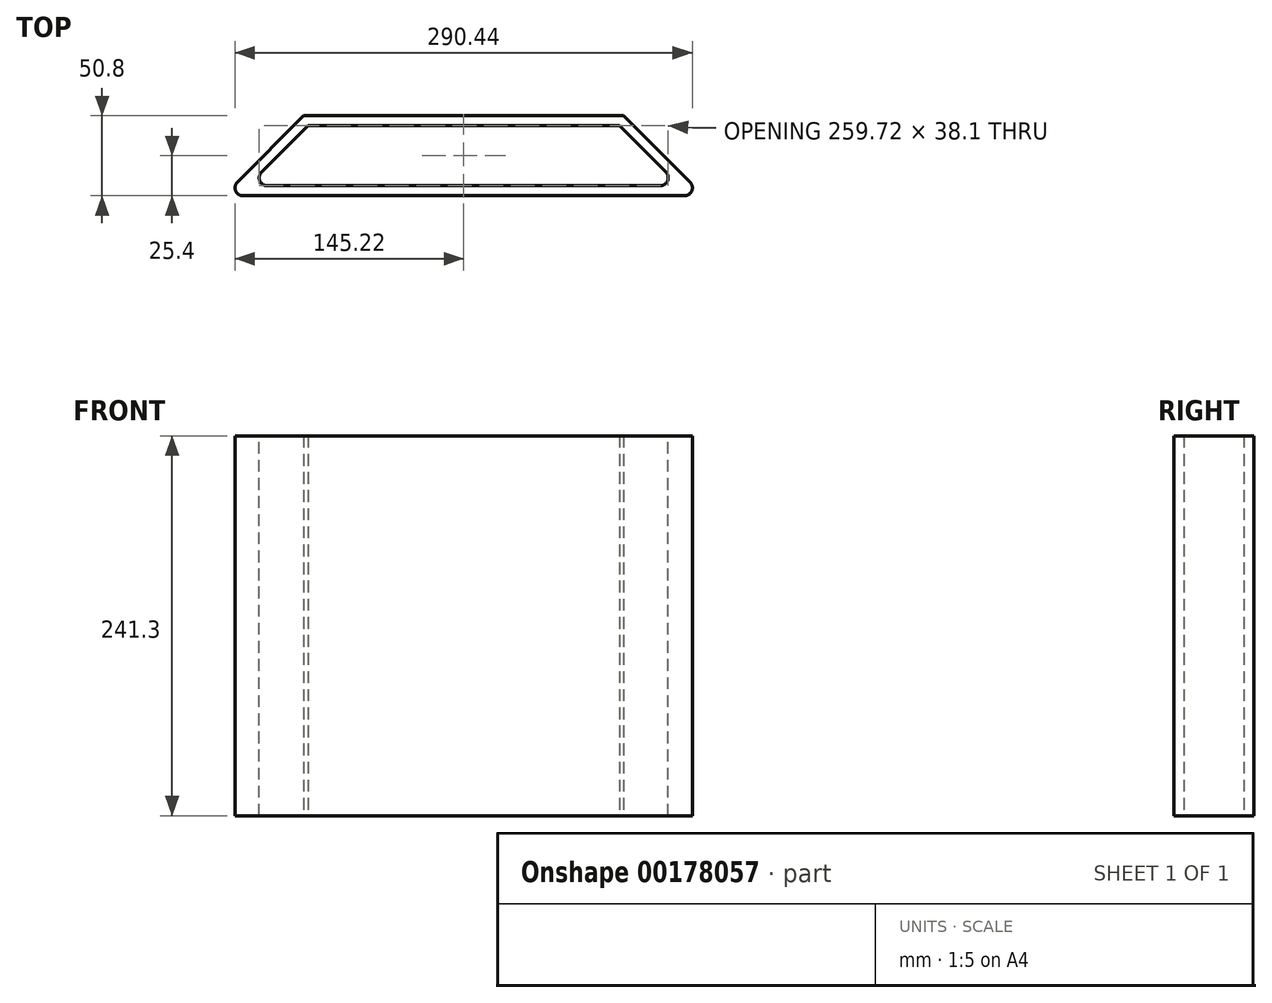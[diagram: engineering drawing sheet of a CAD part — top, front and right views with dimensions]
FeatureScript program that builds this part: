
annotation { "Feature Type Name" : "Feature", "Feature Type Description" : "" }
export const myFeature = defineFeature(function(context is Context, id is Id, definition is map)
    precondition{}
    {
        {
            var Q0;
            Q0=qCreatedBy(makeId("Top.planeOp"),FACE);
            var sketch = newSketch(context, id + "F0", { "sketchPlane" : qUnion([Q0])});
            skLineSegment(sketch, "E0.bottom", {"start": v(0, 0) * mm, "end": v(304.8, 0) * mm});
            skLineSegment(sketch, "E0.top", {"start": v(0, 50.8) * mm, "end": v(304.8, 50.8) * mm, "construction": true});
            skLineSegment(sketch, "E0.left", {"start": v(0, 0) * mm, "end": v(0, 50.8) * mm, "construction": true});
            skLineSegment(sketch, "E0.right", {"start": v(304.8, 0) * mm, "end": v(304.8, 50.8) * mm, "construction": true});
            skLineSegment(sketch, "E1", {"start": v(0, 0) * mm, "end": v(50.8, 50.8) * mm});
            skLineSegment(sketch, "E2", {"start": v(50.8, 50.8) * mm, "end": v(254, 50.8) * mm});
            skLineSegment(sketch, "E3", {"start": v(254, 50.8) * mm, "end": v(304.8, 0) * mm});
            skLineSegment(sketch, "E4", {"start": v(15.33, 6.35) * mm, "end": v(53.43, 44.45) * mm});
            skLineSegment(sketch, "E5", {"start": v(53.43, 44.45) * mm, "end": v(251.37, 44.45) * mm});
            skLineSegment(sketch, "E6", {"start": v(251.37, 44.45) * mm, "end": v(289.47, 6.35) * mm});
            skLineSegment(sketch, "E7", {"start": v(289.47, 6.35) * mm, "end": v(15.33, 6.35) * mm});
            skSolve(sketch);
        }
        {
            var Q0;
            Q0=makeQuery(id+"F0.imprint","IMPRINT",FACE,{"disambiguationData":[TD([[makeQuery(id+"F0.imprint","IMPRINT",EDGE,{"derivedFrom":sQuery(id+"F0.wireOp",EDGE,"E0.bottom")}),1.0]])]});
            extrude(context, id + "F1", {"entities" : qUnion([Q0]), "depth" : 241.3 * mm});
        }
        {
            var Q0;
            Q0=makeQuery(id+"F1.opExtrude","SWEPT_EDGE",EDGE,{"disambiguationData":[OSD([sQuery(id+"F0.wireOp",EDGE,"E0.bottom"),sQuery(id+"F0.wireOp",EDGE,"E1")])]});
            var Q1;
            Q1=makeQuery(id+"F1.opExtrude","SWEPT_EDGE",EDGE,{"disambiguationData":[OSD([sQuery(id+"F0.wireOp",EDGE,"E4"),sQuery(id+"F0.wireOp",EDGE,"E7")])]});
            var Q2;
            Q2=makeQuery(id+"F1.opExtrude","SWEPT_EDGE",EDGE,{"disambiguationData":[OSD([sQuery(id+"F0.wireOp",EDGE,"E0.bottom"),sQuery(id+"F0.wireOp",EDGE,"E3")])]});
            var Q3;
            Q3=makeQuery(id+"F1.opExtrude","SWEPT_EDGE",EDGE,{"disambiguationData":[OSD([sQuery(id+"F0.wireOp",EDGE,"E6"),sQuery(id+"F0.wireOp",EDGE,"E7")])]});
            fillet(context, id + "F2", {"entities" : qUnion([Q0, Q1, Q2, Q3]), "radius" : 5.08 * mm, "tangentPropagation" : true, "allowEdgeOverflow" : false});
        }
    });
